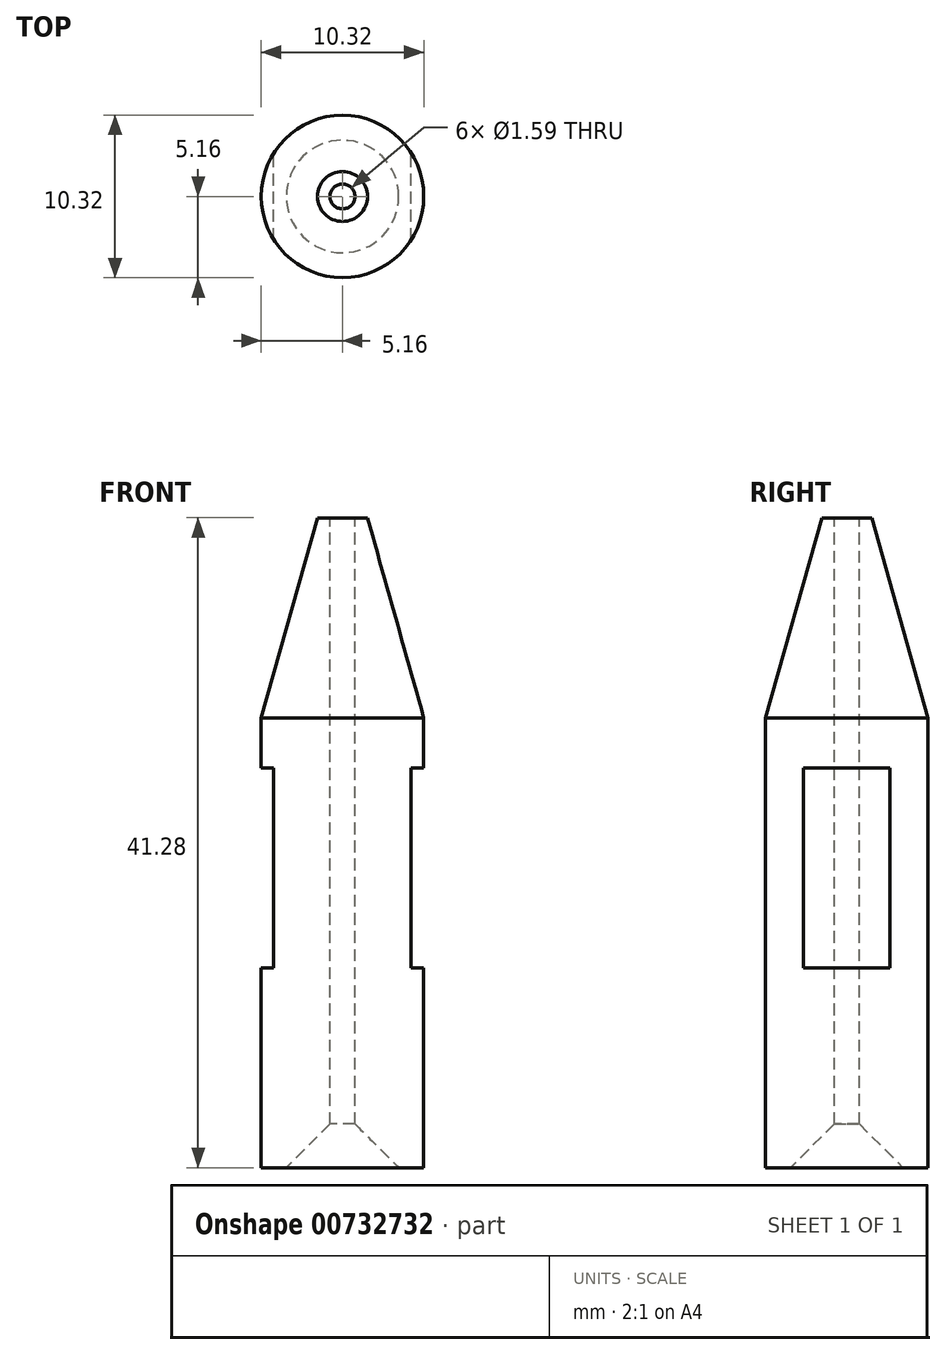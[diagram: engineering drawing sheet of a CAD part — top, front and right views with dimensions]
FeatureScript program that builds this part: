
annotation { "Feature Type Name" : "Feature", "Feature Type Description" : "" }
export const myFeature = defineFeature(function(context is Context, id is Id, definition is map)
    precondition{}
    {
        {
            var Q0;
            Q0=qCreatedBy(makeId("Front.planeOp"),FACE);
            var sketch = newSketch(context, id + "F0", { "sketchPlane" : qUnion([Q0])});
            skLineSegment(sketch, "E0", {"start": v(0, 0) * mm, "end": v(5.16, 0) * mm, "construction": true});
            skLineSegment(sketch, "E1", {"start": v(5.16, 0) * mm, "end": v(5.16, 28.58) * mm});
            skLineSegment(sketch, "E2", {"start": v(0, 46.92) * mm, "end": v(0, 0) * mm, "construction": true});
            skLineSegment(sketch, "E3", {"start": v(5.16, 28.58) * mm, "end": v(0, 46.92) * mm, "construction": true});
            skLineSegment(sketch, "E4", {"start": v(5.16, 28.57) * mm, "end": v(1.59, 41.28) * mm});
            skLineSegment(sketch, "E5", {"start": v(1.59, 41.28) * mm, "end": v(0, 41.28) * mm});
            skLineSegment(sketch, "E6", {"start": v(0.8, 41.28) * mm, "end": v(0.8, 0) * mm});
            skLineSegment(sketch, "E7", {"start": v(0.8, 0) * mm, "end": v(5.16, 0) * mm});
            skLineSegment(sketch, "E8", {"start": v(0.8, 2.78) * mm, "end": v(3.57, 0) * mm});
            skSolve(sketch);
        }
        {
            var Q0;
            Q0=makeQuery(id+"F0.imprint","IMPRINT",FACE,{"disambiguationData":[TD([[makeQuery(id+"F0.imprint","IMPRINT",EDGE,{"derivedFrom":sQuery(id+"F0.wireOp",EDGE,"E1")}),1.0]])]});
            var Q1;
            Q1=sQuery(id+"F0.wireOp",EDGE,"E2");
            revolve(context, id + "F1", {"surfaceOperationType" : NewSurfaceOperationType.NEW, "entities" : qUnion([Q0]), "axis" : qUnion([Q1]), "revolveType" : RevolveType.FULL});
        }
        {
            var Q0;
            Q0=qCreatedBy(makeId("Front.planeOp"),FACE);
            var sketch = newSketch(context, id + "F2", { "sketchPlane" : qUnion([Q0])});
            skLineSegment(sketch, "E9.bottom", {"start": v(-5.16, 25.4) * mm, "end": v(5.16, 25.4) * mm});
            skLineSegment(sketch, "E9.top", {"start": v(-5.16, 12.7) * mm, "end": v(5.16, 12.7) * mm});
            skLineSegment(sketch, "E9.left", {"start": v(-5.16, 25.4) * mm, "end": v(-5.16, 12.7) * mm});
            skLineSegment(sketch, "E9.right", {"start": v(5.16, 25.4) * mm, "end": v(5.16, 12.7) * mm});
            skLineSegment(sketch, "E10", {"start": v(4.37, 25.4) * mm, "end": v(4.37, 12.7) * mm});
            skLineSegment(sketch, "E11", {"start": v(5.16, 12.7) * mm, "end": v(0, 0) * mm, "construction": true});
            skLineSegment(sketch, "E12", {"start": v(0, 0) * mm, "end": v(-5.16, 12.7) * mm, "construction": true});
            skLineSegment(sketch, "E13", {"start": v(-4.37, 12.7) * mm, "end": v(-4.37, 25.4) * mm});
            skSolve(sketch);
        }
        {
            var Q0;
            {var subQ0=sQuery(id+"F2.wireOp",EDGE,"E9.left");Q0=makeQuery(id+"F2.imprint","IMPRINT",FACE,{"disambiguationData":[TD([[makeQuery(id+"F2.imprint","IMPRINT",EDGE,{"derivedFrom":subQ0}),1.0]])]});}
            var Q1;
            {var subQ0=sQuery(id+"F2.wireOp",EDGE,"E9.right");Q1=makeQuery(id+"F2.imprint","IMPRINT",FACE,{"disambiguationData":[TD([[makeQuery(id+"F2.imprint","IMPRINT",EDGE,{"derivedFrom":subQ0}),-1.0]])]});}
            extrude(context, id + "F3", {"entities" : qUnion([Q0, Q1]), "operationType" : NewBodyOperationType.REMOVE, "endBound" : BoundingType.SYMMETRIC, "depth" : 25.4 * mm, "offsetDistance" : 25.4 * mm});
        }
    });
